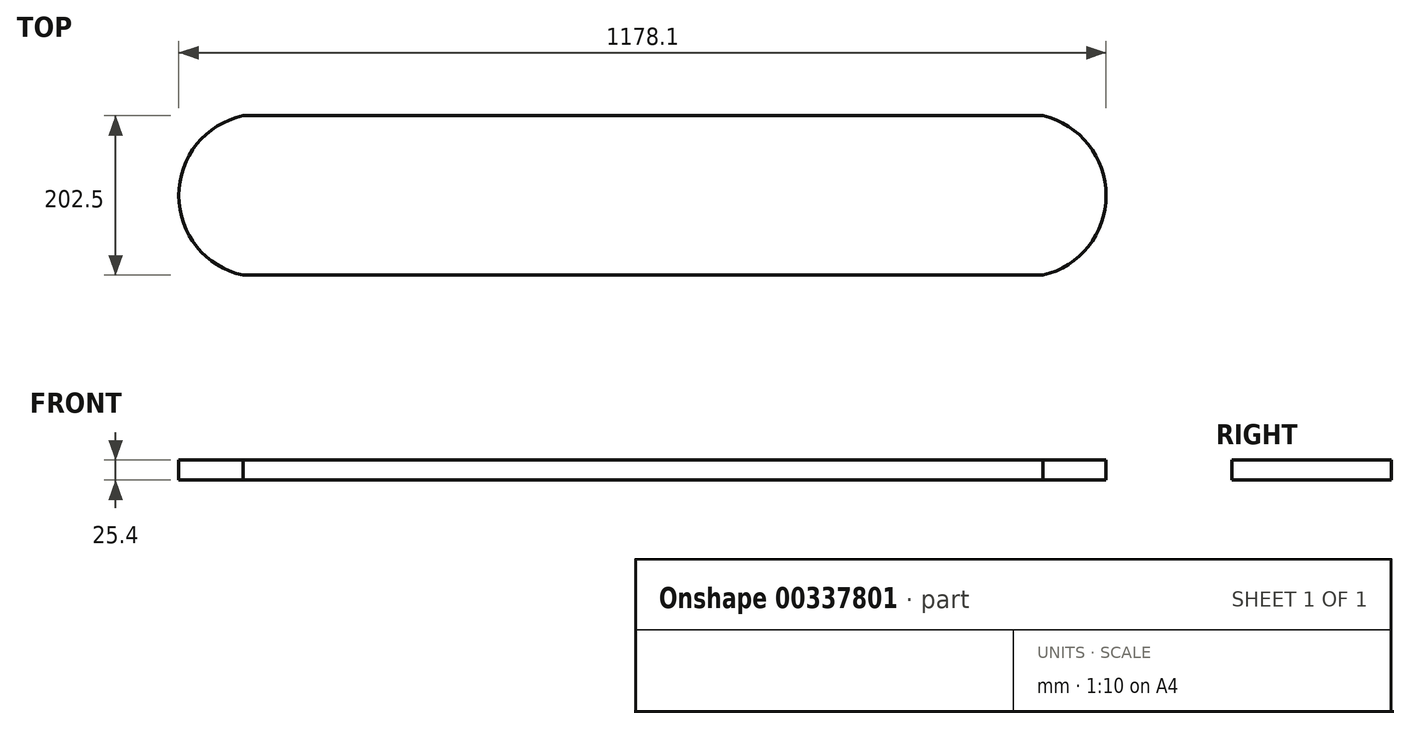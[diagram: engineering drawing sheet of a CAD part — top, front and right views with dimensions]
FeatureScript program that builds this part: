
annotation { "Feature Type Name" : "Feature", "Feature Type Description" : "" }
export const myFeature = defineFeature(function(context is Context, id is Id, definition is map)
    precondition{}
    {
        {
            var Q0;
            Q0=qCreatedBy(makeId("Top.planeOp"),FACE);
            var sketch = newSketch(context, id + "F0", { "sketchPlane" : qUnion([Q0])});
            skLineSegment(sketch, "E0.bottom", {"start": v(-508, 101.25) * mm, "end": v(508, 101.25) * mm});
            skLineSegment(sketch, "E0.top", {"start": v(-508, -101.25) * mm, "end": v(508, -101.25) * mm});
            skLineSegment(sketch, "E0.left", {"start": v(-508, 101.25) * mm, "end": v(-508, -101.25) * mm});
            skLineSegment(sketch, "E0.right", {"start": v(508, 101.25) * mm, "end": v(508, -101.25) * mm});
            skPoint(sketch, "E0.middle", {"position": v(0, 0) * mm});
            skArc(sketch, "E1", {"start": v(-508, 101.25) * mm, "mid": v(-589.78, 0) * mm, "end": v(-508, -101.25) * mm});
            skArc(sketch, "E2", {"start": v(508, -101.25) * mm, "mid": v(588.32, 0) * mm, "end": v(508, 101.25) * mm});
            skSolve(sketch);
        }
        {
            var Q0;
            Q0 = qSketchRegion(id + "F0", true);
            extrude(context, id + "F1", {"entities" : qUnion([Q0]), "depth" : 25.4 * mm});
        }
    });
